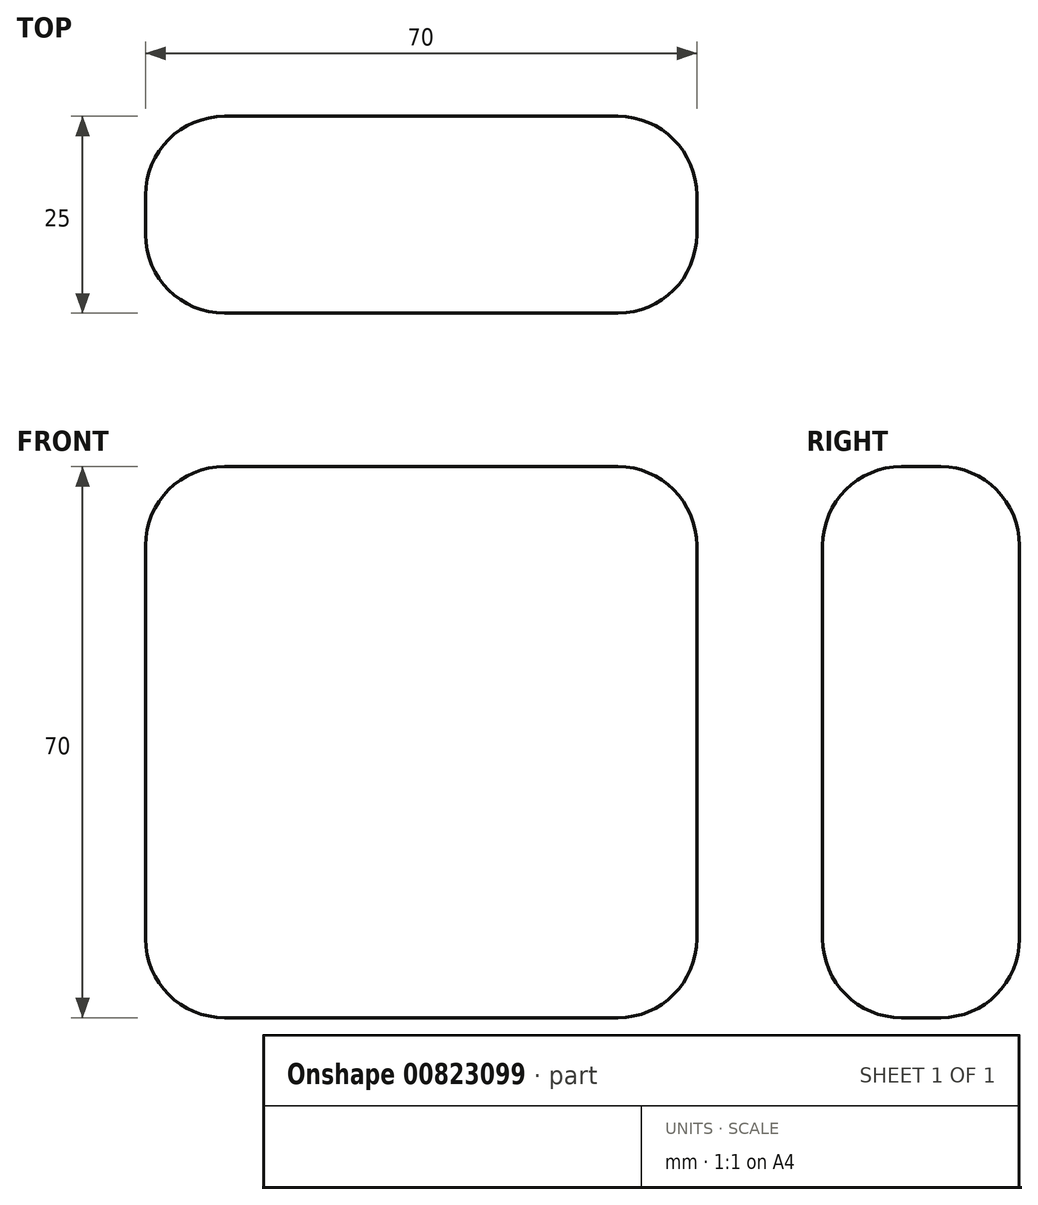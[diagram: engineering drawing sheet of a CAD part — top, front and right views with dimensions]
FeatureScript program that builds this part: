
annotation { "Feature Type Name" : "Feature", "Feature Type Description" : "" }
export const myFeature = defineFeature(function(context is Context, id is Id, definition is map)
    precondition{}
    {
        {
            var Q0;
            Q0=qCreatedBy(makeId("Front.planeOp"),FACE);
            var sketch = newSketch(context, id + "F0", { "sketchPlane" : qUnion([Q0])});
            skLineSegment(sketch, "E0.bottom", {"start": v(-35, 35) * mm, "end": v(35, 35) * mm});
            skLineSegment(sketch, "E0.top", {"start": v(-35, -35) * mm, "end": v(35, -35) * mm});
            skLineSegment(sketch, "E0.left", {"start": v(-35, 35) * mm, "end": v(-35, -35) * mm});
            skLineSegment(sketch, "E0.right", {"start": v(35, 35) * mm, "end": v(35, -35) * mm});
            skSolve(sketch);
        }
        {
            var Q0;
            Q0=makeQuery(id+"F0.imprint","IMPRINT",FACE,{"disambiguationData":[TD([[makeQuery(id+"F0.imprint","IMPRINT",EDGE,{"derivedFrom":sQuery(id+"F0.wireOp",EDGE,"E0.bottom")}),-1.0]])]});
            extrude(context, id + "F1", {"entities" : qUnion([Q0]), "depth" : 25 * mm, "offsetDistance" : 25 * mm});
        }
        {
            var Q0;
            Q0=makeQuery(id+"F1.opExtrude","SWEPT_FACE",FACE,{"disambiguationData":[OSD([sQuery(id+"F0.wireOp",EDGE,"E0.top")])]});
            var Q1;
            Q1=makeQuery(id+"F1.opExtrude","SWEPT_FACE",FACE,{"disambiguationData":[OSD([sQuery(id+"F0.wireOp",EDGE,"E0.right")])]});
            var Q2;
            Q2=makeQuery(id+"F1.opExtrude","SWEPT_FACE",FACE,{"disambiguationData":[OSD([sQuery(id+"F0.wireOp",EDGE,"E0.bottom")])]});
            var Q3;
            Q3=makeQuery(id+"F1.opExtrude","SWEPT_FACE",FACE,{"disambiguationData":[OSD([sQuery(id+"F0.wireOp",EDGE,"E0.left")])]});
            var Q4;
            Q4=makeQuery(id+"F1.opExtrude","CAP_FACE",FACE,{"disambiguationData":[OSD([sQuery(id+"F0.wireOp",EDGE,"E0.bottom"),sQuery(id+"F0.wireOp",EDGE,"E0.top"),sQuery(id+"F0.wireOp",EDGE,"E0.left"),sQuery(id+"F0.wireOp",EDGE,"E0.right")])],"isStart":false});
            fillet(context, id + "F2", {"entities" : qUnion([Q0, Q1, Q2, Q3, Q4]), "radius" : 10 * mm, "tangentPropagation" : true, "allowEdgeOverflow" : false});
        }
    });
